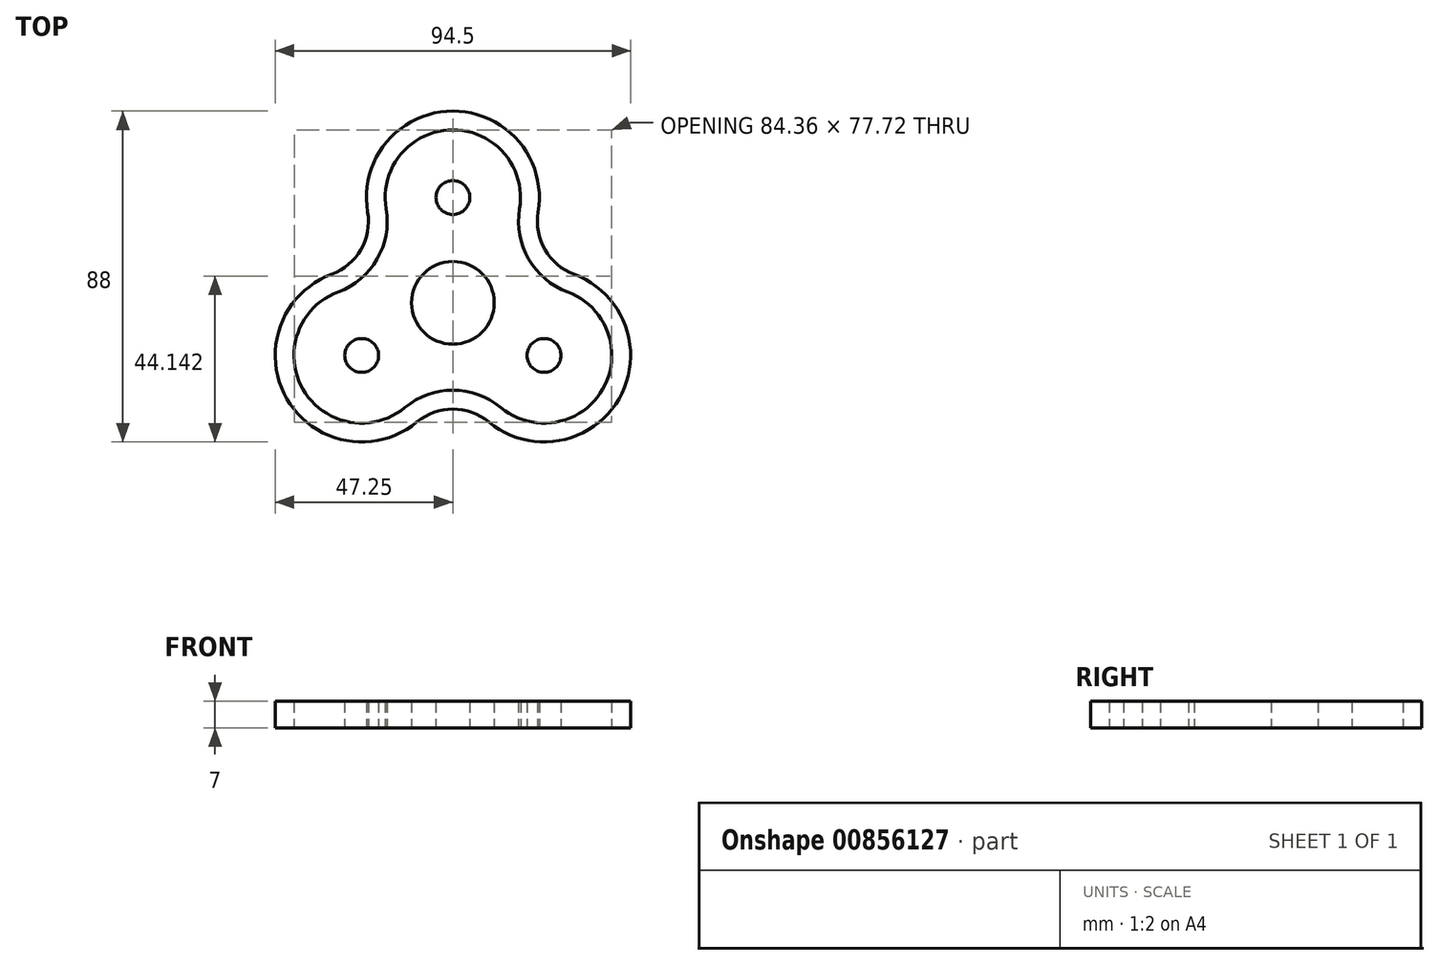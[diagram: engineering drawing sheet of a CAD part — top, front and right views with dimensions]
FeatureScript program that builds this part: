
annotation { "Feature Type Name" : "Feature", "Feature Type Description" : "" }
export const myFeature = defineFeature(function(context is Context, id is Id, definition is map)
    precondition{}
    {
        {
            var Q0;
            Q0=qCreatedBy(makeId("Top.planeOp"),FACE);
            var sketch = newSketch(context, id + "F0", { "sketchPlane" : qUnion([Q0])});
            skCircle(sketch, "E0", {"center": v(0, 0) * mm, "radius": 11 * mm});
            skLineSegment(sketch, "E1", {"start": v(16.38, -9.46) * mm, "end": v(16.75, -9.67) * mm});
            skArc(sketch, "E2", {"start": v(-30.5, 2.88) * mm, "mid": v(-39.84, -23) * mm, "end": v(-12.76, -27.86) * mm});
            skArc(sketch, "E3", {"start": v(12.76, -27.86) * mm, "mid": v(39.84, -23) * mm, "end": v(30.5, 2.88) * mm});
            skArc(sketch, "E4", {"start": v(-30.5, 2.88) * mm, "mid": v(-20.14, 11.63) * mm, "end": v(-17.75, 24.98) * mm});
            skArc(sketch, "E5", {"start": v(12.76, -27.86) * mm, "mid": v(0, -23.26) * mm, "end": v(-12.76, -27.86) * mm});
            skArc(sketch, "E6", {"start": v(17.75, 24.98) * mm, "mid": v(20.14, 11.63) * mm, "end": v(30.5, 2.88) * mm});
            skArc(sketch, "E7.trimOffspring", {"start": v(17.75, 24.98) * mm, "mid": v(0, 46) * mm, "end": v(-17.75, 24.98) * mm});
            skLineSegment(sketch, "E8.trimOffspring", {"start": v(-15.59, -9) * mm, "end": v(-16.75, -9.67) * mm});
            skArc(sketch, "E9.0", {"start": v(22.67, 24.14) * mm, "mid": v(0, 51) * mm, "end": v(-22.67, 24.14) * mm});
            skArc(sketch, "E10.0", {"start": v(-32.25, 7.56) * mm, "mid": v(-24.47, 14.13) * mm, "end": v(-22.67, 24.14) * mm});
            skArc(sketch, "E11.0", {"start": v(-32.25, 7.56) * mm, "mid": v(-44.17, -25.5) * mm, "end": v(-9.57, -31.7) * mm});
            skArc(sketch, "E12.0", {"start": v(9.57, -31.7) * mm, "mid": v(0, -28.26) * mm, "end": v(-9.57, -31.7) * mm});
            skArc(sketch, "E13.0", {"start": v(9.57, -31.7) * mm, "mid": v(44.17, -25.5) * mm, "end": v(32.25, 7.56) * mm});
            skArc(sketch, "E14.0", {"start": v(22.67, 24.14) * mm, "mid": v(24.47, 14.13) * mm, "end": v(32.25, 7.56) * mm});
            skCircle(sketch, "E15", {"center": v(0, 28) * mm, "radius": 4.5 * mm});
            skCircle(sketch, "E16", {"center": v(-24.25, -14) * mm, "radius": 4.5 * mm});
            skCircle(sketch, "E17", {"center": v(24.25, -14) * mm, "radius": 4.5 * mm});
            skSolve(sketch);
        }
        {
            var Q0;
            Q0=makeQuery(id+"F0.imprint","IMPRINT",FACE,{"disambiguationData":[TD([[makeQuery(id+"F0.imprint","IMPRINT",EDGE,{"derivedFrom":sQuery(id+"F0.wireOp",EDGE,"E2")}),-1.0]])]});
            var Q1;
            Q1=makeQuery(id+"F0.imprint","IMPRINT",FACE,{"disambiguationData":[TD([[makeQuery(id+"F0.imprint","IMPRINT",EDGE,{"derivedFrom":sQuery(id+"F0.wireOp",EDGE,"E0")}),1.0]])]});
            var Q2;
            Q2=makeQuery(id+"F0.imprint","IMPRINT",FACE,{"disambiguationData":[TD([[makeQuery(id+"F0.imprint","IMPRINT",EDGE,{"derivedFrom":sQuery(id+"F0.wireOp",EDGE,"E16")}),1.0]])]});
            var Q3;
            Q3=makeQuery(id+"F0.imprint","IMPRINT",FACE,{"disambiguationData":[TD([[makeQuery(id+"F0.imprint","IMPRINT",EDGE,{"derivedFrom":sQuery(id+"F0.wireOp",EDGE,"E17")}),1.0]])]});
            var Q4;
            Q4=makeQuery(id+"F0.imprint","IMPRINT",FACE,{"disambiguationData":[TD([[makeQuery(id+"F0.imprint","IMPRINT",EDGE,{"derivedFrom":sQuery(id+"F0.wireOp",EDGE,"E15")}),1.0]])]});
            extrude(context, id + "F1", {"entities" : qUnion([Q0, Q1, Q2, Q3, Q4]), "depth" : 7 * mm, "offsetDistance" : 25 * mm});
        }
    });
